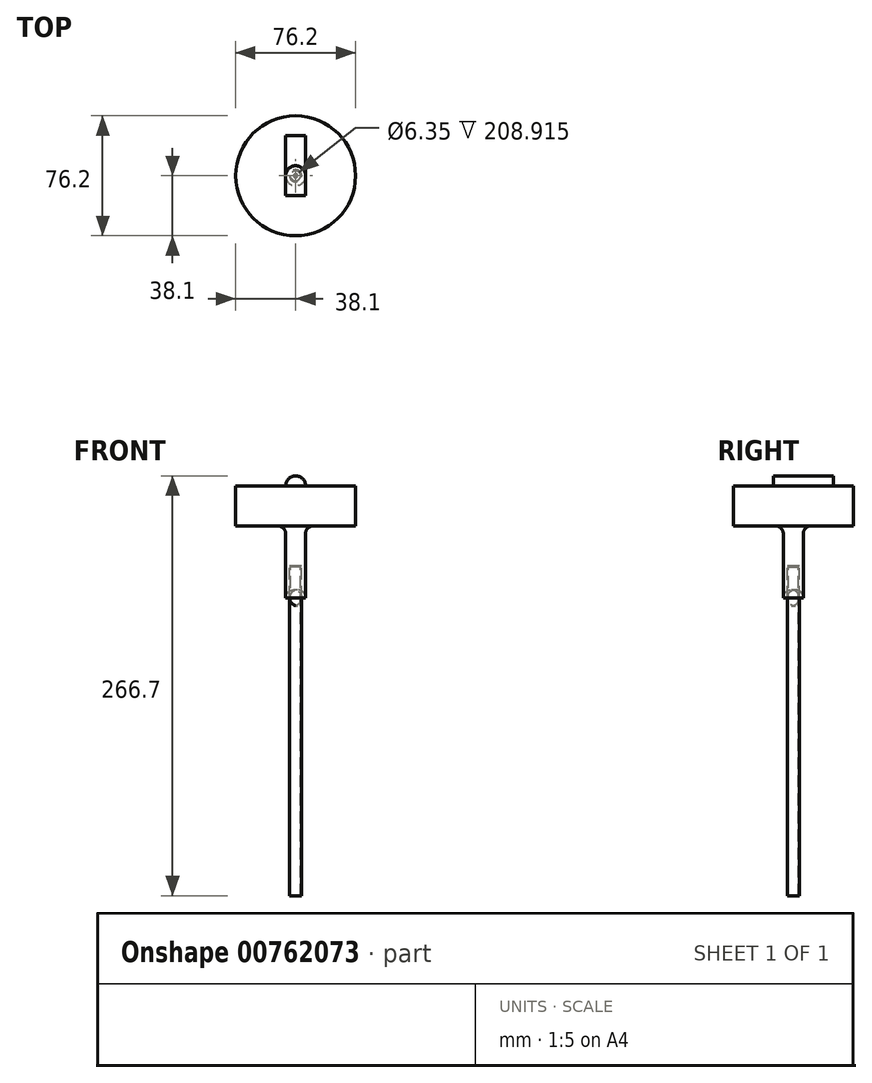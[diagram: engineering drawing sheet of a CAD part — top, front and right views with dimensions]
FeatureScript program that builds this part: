
annotation { "Feature Type Name" : "Feature", "Feature Type Description" : "" }
export const myFeature = defineFeature(function(context is Context, id is Id, definition is map)
    precondition{}
    {
        {
            var Q0;
            Q0=qCreatedBy(makeId("Top.planeOp"),FACE);
            var sketch = newSketch(context, id + "F0", { "sketchPlane" : qUnion([Q0])});
            skCircle(sketch, "E0", {"center": v(0, 0) * mm, "radius": 6.35 * mm});
            skSolve(sketch);
        }
        {
            var Q0;
            Q0=makeQuery(id+"F0.imprint","IMPRINT",FACE,{"disambiguationData":[TD([[makeQuery(id+"F0.imprint","IMPRINT",EDGE,{"derivedFrom":sQuery(id+"F0.wireOp",EDGE,"E0")}),1.0]])]});
            extrude(context, id + "F1", {"entities" : qUnion([Q0]), "oppositeDirection" : true, "depth" : 76.2 * mm, "offsetDistance" : 25.4 * mm});
        }
        {
            var Q0;
            Q0=makeQuery(id+"F1.opExtrude","CAP_FACE",FACE,{"disambiguationData":[OSD([sQuery(id+"F0.wireOp",EDGE,"E0")])],"isStart":false});
            var sketch = newSketch(context, id + "F2", { "sketchPlane" : qUnion([Q0])});
            skCircle(sketch, "E1", {"center": v(0, 0) * mm, "radius": 3.81 * mm});
            skSolve(sketch);
        }
        {
            var Q0;
            Q0=makeQuery(id+"F2.imprint","IMPRINT",FACE,{"disambiguationData":[TD([[makeQuery(id+"F2.imprint","IMPRINT",EDGE,{"derivedFrom":sQuery(id+"F2.wireOp",EDGE,"E1")}),1.0]])]});
            var Q1;
            Q1=sQuery(id+"F2.wireOp",EDGE,"E1");
            extrude(context, id + "F3", {"entities" : qUnion([Q0]), "surfaceEntities" : qUnion([Q1]), "depth" : 184.15 * mm, "offsetDistance" : 25.4 * mm, "hasSecondDirection" : true, "secondDirectionOppositeDirection" : true, "secondDirectionDepth" : 25.4 * mm});
        }
        {
            var Q0;
            Q0=qCreatedBy(makeId("Top.planeOp"),FACE);
            var sketch = newSketch(context, id + "F4", { "sketchPlane" : qUnion([Q0])});
            skCircle(sketch, "E2", {"center": v(0, 0) * mm, "radius": 38.1 * mm});
            skSolve(sketch);
        }
        {
            var Q0;
            Q0 = qSketchRegion(id + "F4", true);
            extrude(context, id + "F5", {"entities" : qUnion([Q0]), "operationType" : NewBodyOperationType.ADD, "oppositeDirection" : true, "depth" : 25.4 * mm, "offsetDistance" : 25.4 * mm});
        }
        {
            var Q0;
            Q0=makeQuery(id+"F1.opExtrude","CAP_EDGE",EDGE,{"disambiguationData":[OSD([sQuery(id+"F0.wireOp",EDGE,"E0")])],"isStart":false});
            var Q1;
            Q1=makeQuery(id+"F1.opExtrude","SWEPT_FACE",FACE,{"disambiguationData":[OSD([sQuery(id+"F0.wireOp",EDGE,"E0")])]});
            fillet(context, id + "F6", {"entities" : qUnion([Q0, Q1]), "radius" : 5.08 * mm, "tangentPropagation" : true, "allowEdgeOverflow" : false});
        }
        {
            var Q0;
            Q0=makeQuery(id+"F5.boolean.opBoolean","MERGE",FACE,{"derivedFrom":[makeQuery(id+"F1.opExtrude","CAP_FACE",FACE,{"disambiguationData":[OSD([sQuery(id+"F0.wireOp",EDGE,"E0")])],"isStart":true}),makeQuery(id+"F5.opExtrude","CAP_FACE",FACE,{"disambiguationData":[OSD([sQuery(id+"F4.wireOp",EDGE,"E2")])],"isStart":true})]});
            var sketch = newSketch(context, id + "F7", { "sketchPlane" : qUnion([Q0])});
            skLineSegment(sketch, "E3", {"start": v(0, 0) * mm, "end": v(0, -25.4) * mm});
            skLineSegment(sketch, "E4.0", {"start": v(-6.35, 12.7) * mm, "end": v(-6.35, -25.4) * mm});
            skLineSegment(sketch, "E5.bottom", {"start": v(0, -25.4) * mm, "end": v(-6.35, -25.4) * mm});
            skLineSegment(sketch, "E5.top", {"start": v(0, 12.7) * mm, "end": v(-6.35, 12.7) * mm});
            skLineSegment(sketch, "E5.left", {"start": v(0, -25.4) * mm, "end": v(0, 12.7) * mm});
            skLineSegment(sketch, "E5.right", {"start": v(-6.35, -25.4) * mm, "end": v(-6.35, 12.7) * mm});
            skSolve(sketch);
        }
        {
            var Q0;
            Q0 = qSketchRegion(id + "F7", true);
            var Q1;
            Q1=sQuery(id+"F7.wireOp",EDGE,"E3");
            revolve(context, id + "F8", {"operationType" : NewBodyOperationType.ADD, "surfaceOperationType" : NewSurfaceOperationType.NEW, "entities" : qUnion([Q0]), "axis" : qUnion([Q1]), "revolveType" : RevolveType.FULL});
        }
        {
            var Q0;
            Q0=makeQuery(id+"F3.opExtrude","CAP_FACE",FACE,{"disambiguationData":[OSD([sQuery(id+"F2.wireOp",EDGE,"E1")])],"isStart":false});
            shell(context, id + "F9", {"entities" : qUnion([Q0]), "thickness" : 0.64 * mm});
        }
        {
            var Q0;
            Q0=makeQuery(id+"F1.opExtrude","SWEPT_BODY",BODY,{"disambiguationData":[OSD([sQuery(id+"F0.wireOp",EDGE,"E0")])]});
            var Q1;
            Q1=makeQuery(id+"F3.opExtrude","SWEPT_BODY",BODY,{"disambiguationData":[OSD([sQuery(id+"F2.wireOp",EDGE,"E1")])]});
            var Q2;
            Q2=makeQuery(id+"F5.opExtrude","CAP_EDGE",EDGE,{"disambiguationData":[OSD([sQuery(id+"F4.wireOp",EDGE,"E2")])],"isStart":true});
            transform(context, id + "F10", {"entities" : qUnion([Q0, Q1]), "transformType" : TransformType.ROTATION, "transformAxis" : qUnion([Q2]), "angle" : 180 * degree, "makeCopy" : false});
        }
    });
